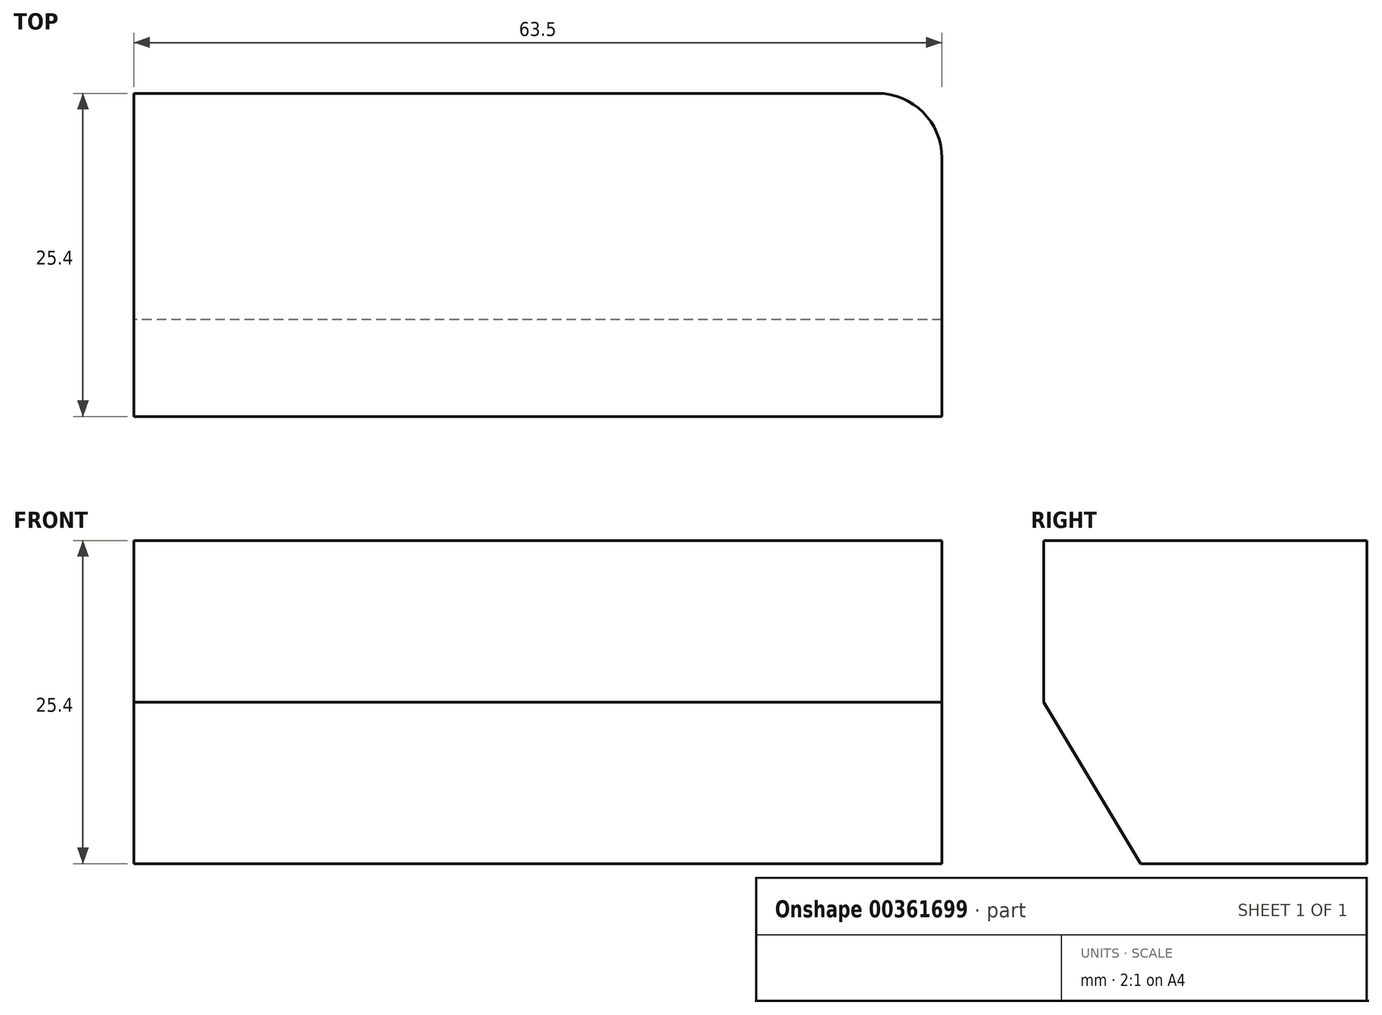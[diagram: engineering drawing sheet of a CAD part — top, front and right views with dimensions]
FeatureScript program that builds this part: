
annotation { "Feature Type Name" : "Feature", "Feature Type Description" : "" }
export const myFeature = defineFeature(function(context is Context, id is Id, definition is map)
    precondition{}
    {
        {
            var Q0;
            Q0=qCreatedBy(makeId("Front.planeOp"),FACE);
            var sketch = newSketch(context, id + "F0", { "sketchPlane" : qUnion([Q0])});
            skLineSegment(sketch, "E0.bottom", {"start": v(31.75, -12.7) * mm, "end": v(-31.75, -12.7) * mm});
            skLineSegment(sketch, "E0.top", {"start": v(31.75, 12.7) * mm, "end": v(-31.75, 12.7) * mm});
            skLineSegment(sketch, "E0.left", {"start": v(31.75, -12.7) * mm, "end": v(31.75, 12.7) * mm});
            skLineSegment(sketch, "E0.right", {"start": v(-31.75, -12.7) * mm, "end": v(-31.75, 12.7) * mm});
            skPoint(sketch, "E0.middle", {"position": v(0, 0) * mm});
            skSolve(sketch);
        }
        {
            var Q0;
            Q0 = qSketchRegion(id + "F0", true);
            extrude(context, id + "F1", {"entities" : qUnion([Q0]), "depth" : 25.4 * mm});
        }
        {
            var Q0;
            Q0=makeQuery(id+"F1.opExtrude","CAP_EDGE",EDGE,{"disambiguationData":[OSD([sQuery(id+"F0.wireOp",EDGE,"E0.left")])],"isStart":true});
            fillet(context, id + "F2", {"entities" : qUnion([Q0]), "radius" : 5.08 * mm, "tangentPropagation" : true, "allowEdgeOverflow" : false});
        }
        {
            var Q0;
            Q0=makeQuery(id+"F1.opExtrude","CAP_EDGE",EDGE,{"disambiguationData":[OSD([sQuery(id+"F0.wireOp",EDGE,"E0.bottom")])],"isStart":false});
            chamfer(context, id + "F3", {"entities" : qUnion([Q0]), "chamferType" : ChamferType.TWO_OFFSETS, "width1" : 7.62 * mm, "oppositeDirection" : false, "width2" : 12.7 * mm, "tangentPropagation" : true});
        }
    });
